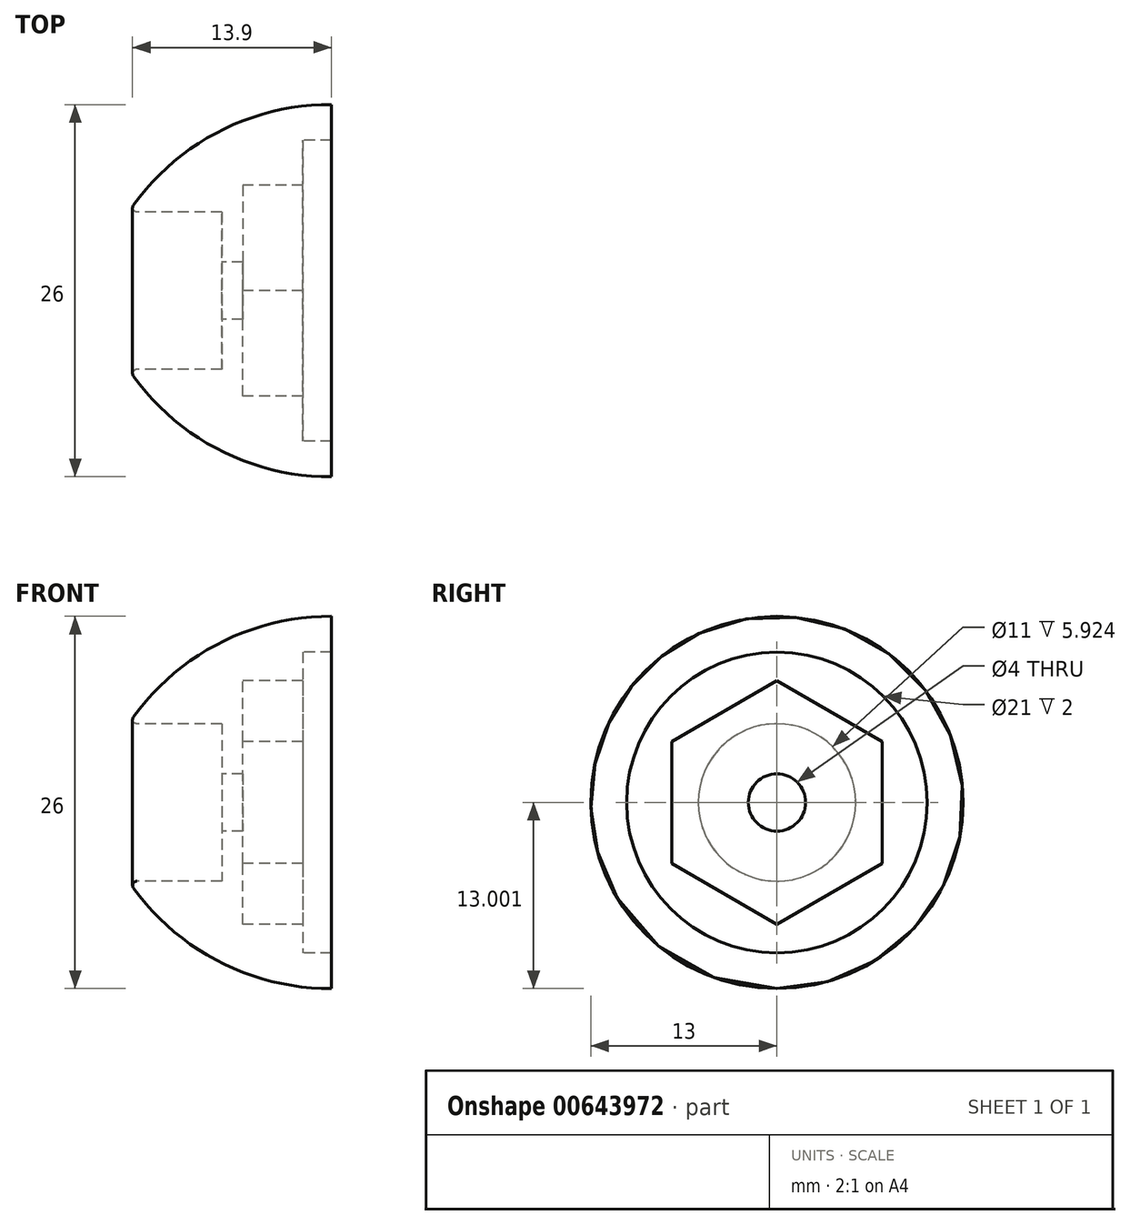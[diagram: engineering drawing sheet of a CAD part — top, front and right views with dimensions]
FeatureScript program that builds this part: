
annotation { "Feature Type Name" : "Feature", "Feature Type Description" : "" }
export const myFeature = defineFeature(function(context is Context, id is Id, definition is map)
    precondition{}
    {
        {
            var Q0;
            Q0=qCreatedBy(makeId("Front.planeOp"),FACE);
            var sketch = newSketch(context, id + "F0", { "sketchPlane" : qUnion([Q0])});
            skLineSegment(sketch, "E0", {"start": v(-16.18, 2.35) * mm, "end": v(-9.68, 2.35) * mm});
            skLineSegment(sketch, "E1", {"start": v(-9.68, 2.35) * mm, "end": v(-9.68, -1.15) * mm});
            skLineSegment(sketch, "E2", {"start": v(-9.68, -1.15) * mm, "end": v(-8.21, -1.15) * mm});
            skLineSegment(sketch, "E3", {"start": v(-8.21, -1.15) * mm, "end": v(-8.21, 5.35) * mm});
            skLineSegment(sketch, "E4", {"start": v(-8.21, 5.35) * mm, "end": v(-4.01, 5.35) * mm});
            skLineSegment(sketch, "E5", {"start": v(-4.01, 5.35) * mm, "end": v(-4.01, 7.35) * mm});
            skLineSegment(sketch, "E6", {"start": v(-4.01, 7.35) * mm, "end": v(-2.01, 7.35) * mm});
            skLineSegment(sketch, "E7", {"start": v(-2.01, 7.35) * mm, "end": v(-2.01, 9.85) * mm});
            skArc(sketch, "E8", {"start": v(-2.01, 9.85) * mm, "mid": v(-10.04, 7.88) * mm, "end": v(-16.18, 2.35) * mm});
            skLineSegment(sketch, "E9", {"start": v(-17.96, -3.15) * mm, "end": v(3, -3.15) * mm, "construction": true});
            skSolve(sketch);
        }
        {
            var Q0;
            Q0=makeQuery(id+"F0.imprint","IMPRINT",FACE,{"disambiguationData":[TD([[makeQuery(id+"F0.imprint","IMPRINT",EDGE,{"derivedFrom":sQuery(id+"F0.wireOp",EDGE,"E0")}),1.0]])]});
            var Q1;
            Q1=sQuery(id+"F0.wireOp",EDGE,"E9");
            revolve(context, id + "F1", {"entities" : qUnion([Q0]), "axis" : qUnion([Q1]), "revolveType" : RevolveType.FULL});
        }
        {
            var Q0;
            Q0=makeQuery(id+"F1.opRevolve","SWEPT_EDGE",EDGE,{"disambiguationData":[OSD([sQuery(id+"F0.wireOp",EDGE,"E0"),sQuery(id+"F0.wireOp",EDGE,"E8")])]});
            fillet(context, id + "F2", {"entities" : qUnion([Q0]), "radius" : 0.3 * mm, "tangentPropagation" : true, "allowEdgeOverflow" : false});
        }
        {
            var Q0;
            Q0=makeQuery(id+"F1.opRevolve","SWEPT_FACE",FACE,{"disambiguationData":[OSD([sQuery(id+"F0.wireOp",EDGE,"E3")])]});
            var sketch = newSketch(context, id + "F3", { "sketchPlane" : qUnion([Q0])});
            skCircle(sketch, "E10.cCircle", {"center": v(0, -3.15) * mm, "radius": 8.5 * mm});
            skLineSegment(sketch, "E10.0", {"start": v(0, 5.35) * mm, "end": v(7.36, 1.1) * mm});
            skLineSegment(sketch, "E10.1", {"start": v(7.36, 1.1) * mm, "end": v(7.36, -7.4) * mm});
            skLineSegment(sketch, "E10.2", {"start": v(7.36, -7.4) * mm, "end": v(0, -11.65) * mm});
            skLineSegment(sketch, "E10.3", {"start": v(0, -11.65) * mm, "end": v(-7.36, -7.4) * mm});
            skLineSegment(sketch, "E10.4", {"start": v(-7.36, -7.4) * mm, "end": v(-7.36, 1.1) * mm});
            skLineSegment(sketch, "E10.5", {"start": v(-7.36, 1.1) * mm, "end": v(0, 5.35) * mm});
            skSolve(sketch);
        }
        {
            var Q0;
            {var subQ0=sQuery(id+"F3.wireOp",EDGE,"E10.5");Q0=makeQuery(id+"F3.imprint","IMPRINT",FACE,{"disambiguationData":[TD([[makeQuery(id+"F3.imprint","IMPRINT",EDGE,{"derivedFrom":subQ0}),1.0]])]});}
            var Q1;
            {var subQ0=sQuery(id+"F3.wireOp",EDGE,"E10.0");Q1=makeQuery(id+"F3.imprint","IMPRINT",FACE,{"disambiguationData":[TD([[makeQuery(id+"F3.imprint","IMPRINT",EDGE,{"derivedFrom":subQ0}),1.0]])]});}
            var Q2;
            {var subQ0=sQuery(id+"F3.wireOp",EDGE,"E10.1");Q2=makeQuery(id+"F3.imprint","IMPRINT",FACE,{"disambiguationData":[TD([[makeQuery(id+"F3.imprint","IMPRINT",EDGE,{"derivedFrom":subQ0}),1.0]])]});}
            var Q3;
            {var subQ0=sQuery(id+"F3.wireOp",EDGE,"E10.4");Q3=makeQuery(id+"F3.imprint","IMPRINT",FACE,{"disambiguationData":[TD([[makeQuery(id+"F3.imprint","IMPRINT",EDGE,{"derivedFrom":subQ0}),1.0]])]});}
            var Q4;
            {var subQ0=sQuery(id+"F3.wireOp",EDGE,"E10.3");Q4=makeQuery(id+"F3.imprint","IMPRINT",FACE,{"disambiguationData":[TD([[makeQuery(id+"F3.imprint","IMPRINT",EDGE,{"derivedFrom":subQ0}),1.0]])]});}
            var Q5;
            {var subQ0=sQuery(id+"F3.wireOp",EDGE,"E10.2");Q5=makeQuery(id+"F3.imprint","IMPRINT",FACE,{"disambiguationData":[TD([[makeQuery(id+"F3.imprint","IMPRINT",EDGE,{"derivedFrom":subQ0}),1.0]])]});}
            extrude(context, id + "F4", {"entities" : qUnion([Q0, Q1, Q2, Q3, Q4, Q5]), "operationType" : NewBodyOperationType.ADD, "depth" : 4.2 * mm, "offsetDistance" : 25 * mm});
        }
    });
